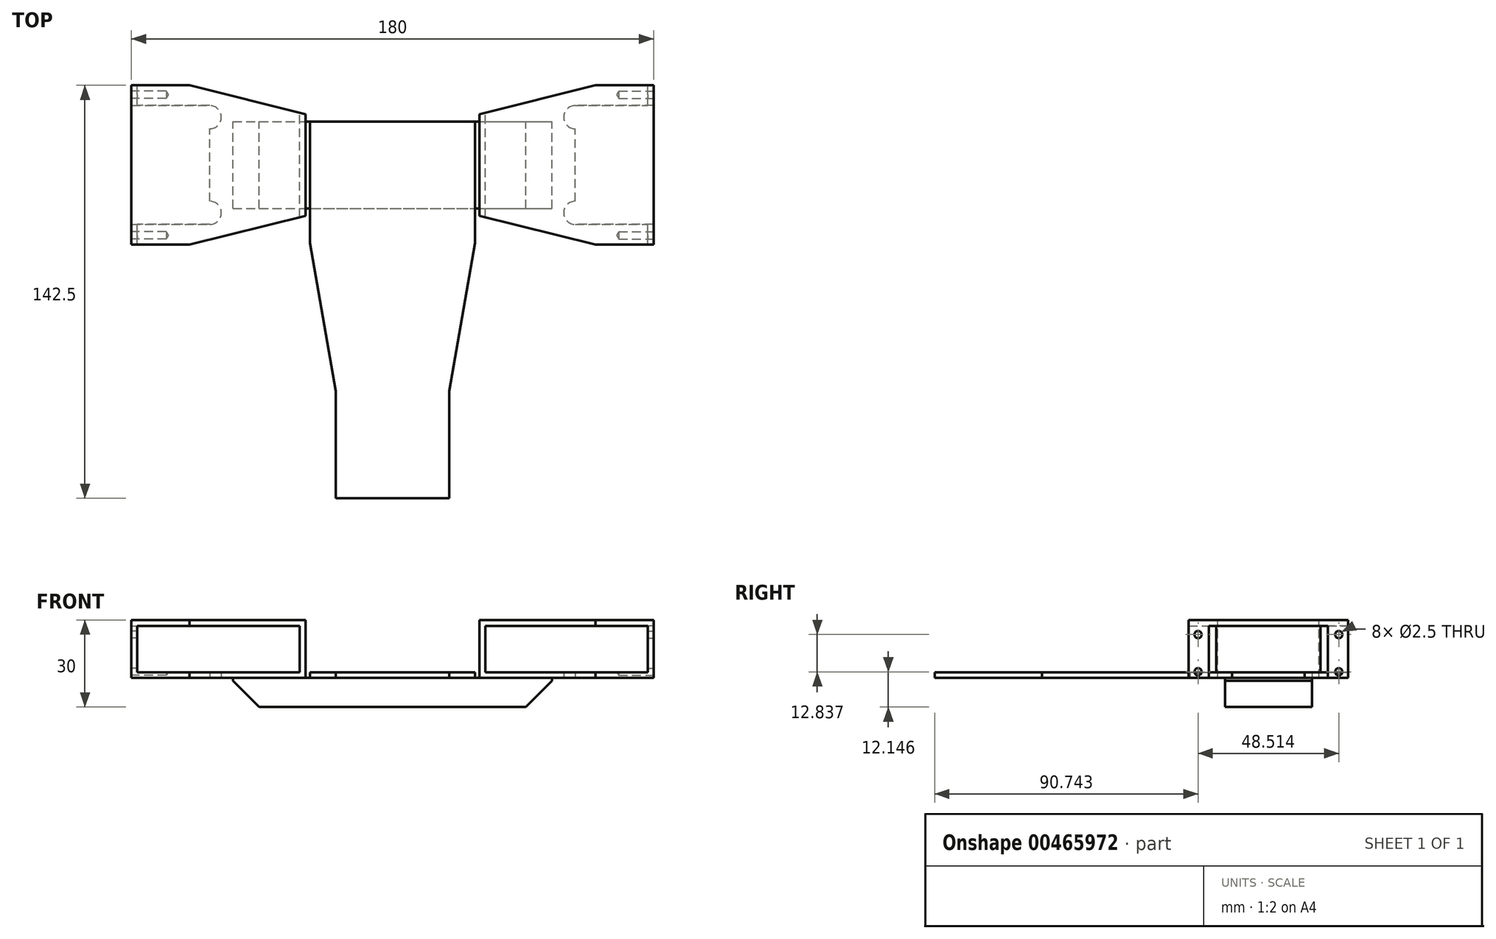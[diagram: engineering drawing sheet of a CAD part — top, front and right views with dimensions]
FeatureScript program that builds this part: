
annotation { "Feature Type Name" : "Feature", "Feature Type Description" : "" }
export const myFeature = defineFeature(function(context is Context, id is Id, definition is map)
    precondition{}
    {
        {
            var Q0;
            Q0=qCreatedBy(makeId("Front.planeOp"),FACE);
            var sketch = newSketch(context, id + "F0", { "sketchPlane" : qUnion([Q0])});
            skLineSegment(sketch, "E0.bottom", {"start": v(-90, 20) * mm, "end": v(-30, 20) * mm});
            skLineSegment(sketch, "E0.top", {"start": v(-90, 0) * mm, "end": v(-30, 0) * mm});
            skLineSegment(sketch, "E0.left", {"start": v(-90, 20) * mm, "end": v(-90, 0) * mm});
            skLineSegment(sketch, "E0.right", {"start": v(-30, 20) * mm, "end": v(-30, 0) * mm});
            skLineSegment(sketch, "E1.bottom", {"start": v(30, 20) * mm, "end": v(90, 20) * mm});
            skLineSegment(sketch, "E1.top", {"start": v(30, 0) * mm, "end": v(90, 0) * mm});
            skLineSegment(sketch, "E1.left", {"start": v(30, 20) * mm, "end": v(30, 0) * mm});
            skLineSegment(sketch, "E1.right", {"start": v(90, 20) * mm, "end": v(90, 0) * mm});
            skLineSegment(sketch, "E2.bottom", {"start": v(-55, 0) * mm, "end": v(55, 0) * mm});
            skLineSegment(sketch, "E2.top", {"start": v(-46, -10) * mm, "end": v(46, -10) * mm});
            skLineSegment(sketch, "E2.left", {"start": v(-55, 0) * mm, "end": v(-55, -1) * mm});
            skLineSegment(sketch, "E2.right", {"start": v(55, 0) * mm, "end": v(55, -1) * mm});
            skLineSegment(sketch, "E3", {"start": v(-55, -1) * mm, "end": v(-46, -10) * mm});
            skLineSegment(sketch, "E4", {"start": v(46, -10) * mm, "end": v(55, -1) * mm});
            skLineSegment(sketch, "E5.0", {"start": v(-88, 18) * mm, "end": v(-32, 18) * mm});
            skLineSegment(sketch, "E5.1", {"start": v(-88, 18) * mm, "end": v(-88, 2) * mm});
            skLineSegment(sketch, "E5.2", {"start": v(-88, 2) * mm, "end": v(-32, 2) * mm});
            skLineSegment(sketch, "E5.3", {"start": v(-32, 18) * mm, "end": v(-32, 2) * mm});
            skLineSegment(sketch, "E6.0", {"start": v(32, 18) * mm, "end": v(88, 18) * mm});
            skLineSegment(sketch, "E6.1", {"start": v(32, 18) * mm, "end": v(32, 2) * mm});
            skLineSegment(sketch, "E6.2", {"start": v(32, 2) * mm, "end": v(88, 2) * mm});
            skLineSegment(sketch, "E6.3", {"start": v(88, 18) * mm, "end": v(88, 2) * mm});
            skSolve(sketch);
        }
        {
            var Q0;
            Q0=makeQuery(id+"F0.imprint","IMPRINT",FACE,{"disambiguationData":[TD([[makeQuery(id+"F0.imprint","IMPRINT",EDGE,{"derivedFrom":sQuery(id+"F0.wireOp",EDGE,"E0.bottom")}),-1.0]])]});
            var Q1;
            Q1=makeQuery(id+"F0.imprint","IMPRINT",FACE,{"disambiguationData":[TD([[makeQuery(id+"F0.imprint","IMPRINT",EDGE,{"derivedFrom":sQuery(id+"F0.wireOp",EDGE,"E1.bottom")}),-1.0]])]});
            extrude(context, id + "F1", {"entities" : qUnion([Q0, Q1]), "endBound" : BoundingType.SYMMETRIC, "depth" : 55 * mm});
        }
        {
            var Q0;
            Q0=makeQuery(id+"F0.imprint","IMPRINT",FACE,{"disambiguationData":[TD([[makeQuery(id+"F0.imprint","IMPRINT",EDGE,{"derivedFrom":sQuery(id+"F0.wireOp",EDGE,"E2.top")}),1.0]])]});
            extrude(context, id + "F2", {"entities" : qUnion([Q0]), "endBound" : BoundingType.SYMMETRIC, "depth" : 30 * mm});
        }
        {
            var Q0;
            Q0=makeQuery(id+"F1.opExtrude","SWEPT_FACE",FACE,{"disambiguationData":[OSD([sQuery(id+"F0.wireOp",EDGE,"E0.bottom")])]});
            var sketch = newSketch(context, id + "F3", { "sketchPlane" : qUnion([Q0])});
            skLineSegment(sketch, "E7", {"start": v(-70, 27.5) * mm, "end": v(-30, 17.5) * mm});
            skLineSegment(sketch, "E8", {"start": v(-30, 17.5) * mm, "end": v(-30, 27.5) * mm});
            skLineSegment(sketch, "E9", {"start": v(-30, 27.5) * mm, "end": v(-70, 27.5) * mm});
            skLineSegment(sketch, "E10", {"start": v(-30, -27.5) * mm, "end": v(-70, -27.5) * mm});
            skLineSegment(sketch, "E11", {"start": v(-70, -27.5) * mm, "end": v(-30, -17.5) * mm});
            skLineSegment(sketch, "E12", {"start": v(-30, -17.5) * mm, "end": v(-30, -27.5) * mm});
            skLineSegment(sketch, "E13.MirrorCS", {"start": v(70, 27.5) * mm, "end": v(30, 17.5) * mm});
            skLineSegment(sketch, "E14.MirrorCS", {"start": v(30, 17.5) * mm, "end": v(30, 27.5) * mm});
            skLineSegment(sketch, "E15.MirrorCS", {"start": v(30, 27.5) * mm, "end": v(70, 27.5) * mm});
            skLineSegment(sketch, "E16.MirrorCS", {"start": v(30, -17.5) * mm, "end": v(30, -27.5) * mm});
            skLineSegment(sketch, "E17.MirrorCS", {"start": v(70, -27.5) * mm, "end": v(30, -17.5) * mm});
            skLineSegment(sketch, "E18.MirrorCS", {"start": v(30, -27.5) * mm, "end": v(70, -27.5) * mm});
            skSolve(sketch);
        }
        {
            var Q0;
            Q0 = qSketchRegion(id + "F3", true);
            extrude(context, id + "F4", {"entities" : qUnion([Q0]), "operationType" : NewBodyOperationType.REMOVE, "endBound" : BoundingType.THROUGH_ALL, "oppositeDirection" : true, "depth" : 25 * mm});
        }
        {
            var Q0;
            Q0=makeQuery(id+"F1.opExtrude","SWEPT_FACE",FACE,{"disambiguationData":[OSD([sQuery(id+"F0.wireOp",EDGE,"E0.top"),sQuery(id+"F0.wireOp",EDGE,"E2.bottom")])]});
            var sketch = newSketch(context, id + "F5", { "sketchPlane" : qUnion([Q0])});
            skLineSegment(sketch, "E19.bottom", {"start": v(-90, 20.5) * mm, "end": v(-63, 20.5) * mm});
            skLineSegment(sketch, "E19.top", {"start": v(-90, -20.5) * mm, "end": v(-63, -20.5) * mm});
            skLineSegment(sketch, "E19.left", {"start": v(-90, 20.5) * mm, "end": v(-90, -20.5) * mm});
            skLineSegment(sketch, "E19.right", {"start": v(-63, 12.5) * mm, "end": v(-63, -12.5) * mm});
            skLineSegment(sketch, "E20.bottom", {"start": v(-90, 20.5) * mm, "end": v(-90, 20.5) * mm});
            skLineSegment(sketch, "E20.top", {"start": v(-90, -20.5) * mm, "end": v(-90, -20.5) * mm});
            skArc(sketch, "E21", {"start": v(-63, 12.5) * mm, "mid": v(-59, 16.5) * mm, "end": v(-63, 20.5) * mm});
            skArc(sketch, "E22", {"start": v(-63, -20.5) * mm, "mid": v(-59, -16.5) * mm, "end": v(-63, -12.5) * mm});
            skSolve(sketch);
        }
        {
            var Q0;
            Q0 = qSketchRegion(id + "F5", true);
            var Q1;
            Q1=makeQuery(id+"F1.opExtrude","SWEPT_FACE",FACE,{"disambiguationData":[OSD([sQuery(id+"F0.wireOp",EDGE,"E5.0")])]});
            extrude(context, id + "F6", {"entities" : qUnion([Q0]), "operationType" : NewBodyOperationType.REMOVE, "endBound" : BoundingType.UP_TO_SURFACE, "oppositeDirection" : true, "endBoundEntityFace" : qUnion([Q1]), "depth" : 25 * mm});
        }
        {
            var Q0;
            Q0=makeQuery(id+"F1.opExtrude","SWEPT_FACE",FACE,{"disambiguationData":[OSD([sQuery(id+"F0.wireOp",EDGE,"E0.left")])]});
            var sketch = newSketch(context, id + "F7", { "sketchPlane" : qUnion([Q0])});
            skPoint(sketch, "E23", {"position": v(-24.26, 14.98) * mm});
            skPoint(sketch, "E24", {"position": v(-24.26, 2.15) * mm});
            skPoint(sketch, "E25", {"position": v(24.26, 14.98) * mm});
            skPoint(sketch, "E26", {"position": v(24.26, 2.15) * mm});
            skLineSegment(sketch, "E27", {"start": v(-20.5, 9) * mm, "end": v(20.5, 9) * mm});
            skSolve(sketch);
        }
        {
            var Q0;
            Q0=makeQuery(id+"F1.opExtrude","SWEPT_BODY",BODY,{"disambiguationData":[OSD([sQuery(id+"F0.wireOp",EDGE,"E1.bottom"),sQuery(id+"F0.wireOp",EDGE,"E1.top"),sQuery(id+"F0.wireOp",EDGE,"E1.left"),sQuery(id+"F0.wireOp",EDGE,"E1.right"),sQuery(id+"F0.wireOp",EDGE,"E2.bottom"),sQuery(id+"F0.wireOp",EDGE,"E6.0"),sQuery(id+"F0.wireOp",EDGE,"E6.1"),sQuery(id+"F0.wireOp",EDGE,"E6.2"),sQuery(id+"F0.wireOp",EDGE,"E6.3")])]});
            deleteBodies(context, id + "F8", {"entities" : qUnion([Q0])});
        }
        {
            var Q0;
            Q0=sQuery(id+"F7.wireOp",VERTEX,"E23");
            var Q1;
            Q1=sQuery(id+"F7.wireOp",VERTEX,"E24");
            var Q2;
            Q2=sQuery(id+"F7.wireOp",VERTEX,"E25");
            var Q3;
            Q3=sQuery(id+"F7.wireOp",VERTEX,"E26");
            var Q4;
            Q4=makeQuery(id+"F1.opExtrude","SWEPT_BODY",BODY,{"disambiguationData":[OSD([sQuery(id+"F0.wireOp",EDGE,"E0.bottom"),sQuery(id+"F0.wireOp",EDGE,"E0.top"),sQuery(id+"F0.wireOp",EDGE,"E0.left"),sQuery(id+"F0.wireOp",EDGE,"E0.right"),sQuery(id+"F0.wireOp",EDGE,"E2.bottom"),sQuery(id+"F0.wireOp",EDGE,"E5.0"),sQuery(id+"F0.wireOp",EDGE,"E5.1"),sQuery(id+"F0.wireOp",EDGE,"E5.2"),sQuery(id+"F0.wireOp",EDGE,"E5.3")])]});
            hole(context, id + "F9", {"style" : HoleStyle.SIMPLE, "endStyle" : HoleEndStyle.BLIND, "holeDiameter" : 2.5 * mm, "holeDepth" : 12 * mm, "isTappedThrough" : true, "tappedDepth" : 12 * mm, "tapClearance" : 3, "locations" : qUnion([Q0, Q1, Q2, Q3]), "scope" : qUnion([Q4])});
        }
        {
            var Q0;
            Q0=makeQuery(id+"F2.opExtrude","SWEPT_FACE",FACE,{"disambiguationData":[OSD([sQuery(id+"F0.wireOp",EDGE,"E2.bottom")])]});
            var sketch = newSketch(context, id + "F10", { "sketchPlane" : qUnion([Q0])});
            skLineSegment(sketch, "E28", {"start": v(-28.5, 15) * mm, "end": v(-28.5, -27) * mm});
            skLineSegment(sketch, "E29", {"start": v(-28.5, -27) * mm, "end": v(-19.5, -78) * mm});
            skLineSegment(sketch, "E30", {"start": v(-19.5, -78) * mm, "end": v(-19.5, -115) * mm});
            skLineSegment(sketch, "E31", {"start": v(-19.5, -115) * mm, "end": v(19.5, -115) * mm});
            skLineSegment(sketch, "E32", {"start": v(19.5, -115) * mm, "end": v(19.5, -78) * mm});
            skLineSegment(sketch, "E33", {"start": v(19.5, -78) * mm, "end": v(28.5, -27) * mm});
            skLineSegment(sketch, "E34", {"start": v(28.5, -27) * mm, "end": v(28.5, 15) * mm});
            skLineSegment(sketch, "E35", {"start": v(28.5, 15) * mm, "end": v(-28.5, 15) * mm});
            skSolve(sketch);
        }
        {
            var Q0;
            Q0 = qSketchRegion(id + "F10", true);
            extrude(context, id + "F11", {"entities" : qUnion([Q0]), "operationType" : NewBodyOperationType.ADD, "depth" : 2 * mm});
        }
        {
            var Q0;
            Q0=makeQuery(id+"F1.opExtrude","SWEPT_BODY",BODY,{"disambiguationData":[OSD([sQuery(id+"F0.wireOp",EDGE,"E0.bottom"),sQuery(id+"F0.wireOp",EDGE,"E0.top"),sQuery(id+"F0.wireOp",EDGE,"E0.left"),sQuery(id+"F0.wireOp",EDGE,"E0.right"),sQuery(id+"F0.wireOp",EDGE,"E2.bottom"),sQuery(id+"F0.wireOp",EDGE,"E5.0"),sQuery(id+"F0.wireOp",EDGE,"E5.1"),sQuery(id+"F0.wireOp",EDGE,"E5.2"),sQuery(id+"F0.wireOp",EDGE,"E5.3")])]});
            var Q1;
            Q1=qCreatedBy(makeId("Right.planeOp"),FACE);
            mirror(context, id + "F12", {"operationType" : NewBodyOperationType.ADD, "entities" : qUnion([Q0]), "mirrorPlane" : qUnion([Q1])});
        }
    });
